# Revit family: Sanitary_Shower-Trays_Sanindusa_Piano_Smooth-Surface-Shower-Tray-90x90
name_source: partatom
category: Plumbing Fixtures
revit_build: Autodesk Revit 2018 (Build: 20170223_1515(x64)
units: mm (PartAtom-declared; Revit-internal decimal feet)

## family parameters
Cut with Voids When Loaded = No
Host = Face
Part Type = Normal
Room Calculation Point = No
Round Connector Dimension = Use Diameter
Shared = No

## types (1)
- Sanitary_Shower-Trays_Sanindusa_Piano_Smooth-Surface-Shower-Tray-90x90
    AssetType = Fixed
    CodePerformance = "EN 14527:2006 / A1:2010
CL 2 "
    Color = white
    Constituents = 48711-90 shower tray drain (not included)
    Default Elevation = 1219 mm
    Description = Installation or waste water appliance that emits a spray of water to wash the human body (BS6100)
    DrainSize = 90 mm  [stored 0.295276 ft]
    Element Type = SHOWER: Installation or waste water appliance that emits a spray of water to wash the human body (BS6100)
    Features = Domestic and commercial use.  Contemporary design. Range with various sizes and depths available.
    Finish = gloss
    HasTray = TRUE
    Installation Instructions = https://www.tec.sanindusa.pt
    InstallationDate = 1900-12-31T23:59:59
    Manufacturer = Sanindusa
    ManufacturerName = Sanindusa
    ManufacturerURL = www.tec.sanindusa.pt
    Material = "3,2 mm acrylic sheet, reinforced with polyester resins, fiberglass and
8 mm wood chipboard in the bottom."
    Model = 8035600000
    ModelNumber = 8035600000
    ModelReference = Piano
    MountingType = AboveTheFloor
    Name = 90x90x7.5 piano smooth surface shower tray
    NominalHeight = 75 mm
    NominalLength = 900 mm  [stored 2.95276 ft]
    NominalWidth = 900 mm  [stored 2.95276 ft]
    Non-slip surface = FALSE
    Pre-defined type (IFC) = SHOWER
    ProductInformation = https://www.tec.sanindusa.pt
    ProductionYear = 2019
    Shape = square
    Size = 90x90
    Type (IFC) = IfcSanitaryTerminalType
    URL = www.tec.sanindusa.pt
    Uniclass2015Code = Pr_40_20_06_84
    Uniclass2015Title = Shower trays
    Uniclass2015Version = Products v1.6
    Version = 1
    WarrantyDescription = https://www.tec.sanindusa.pt
    WarrantyDurationParts = 5
    WarrantyStartDate = 1900-12-31T23:59:59
    Waste Connection = Yes
    Weight = 13.00 kg

note: [stored X ft] marks values corroborated as IEEE doubles in the binary element streams (Revit-internal decimal feet)

## geometry (parser evidence)
native form markers: Extrusion x1, Sweep x7
no freeform markers — native parametric forms only
